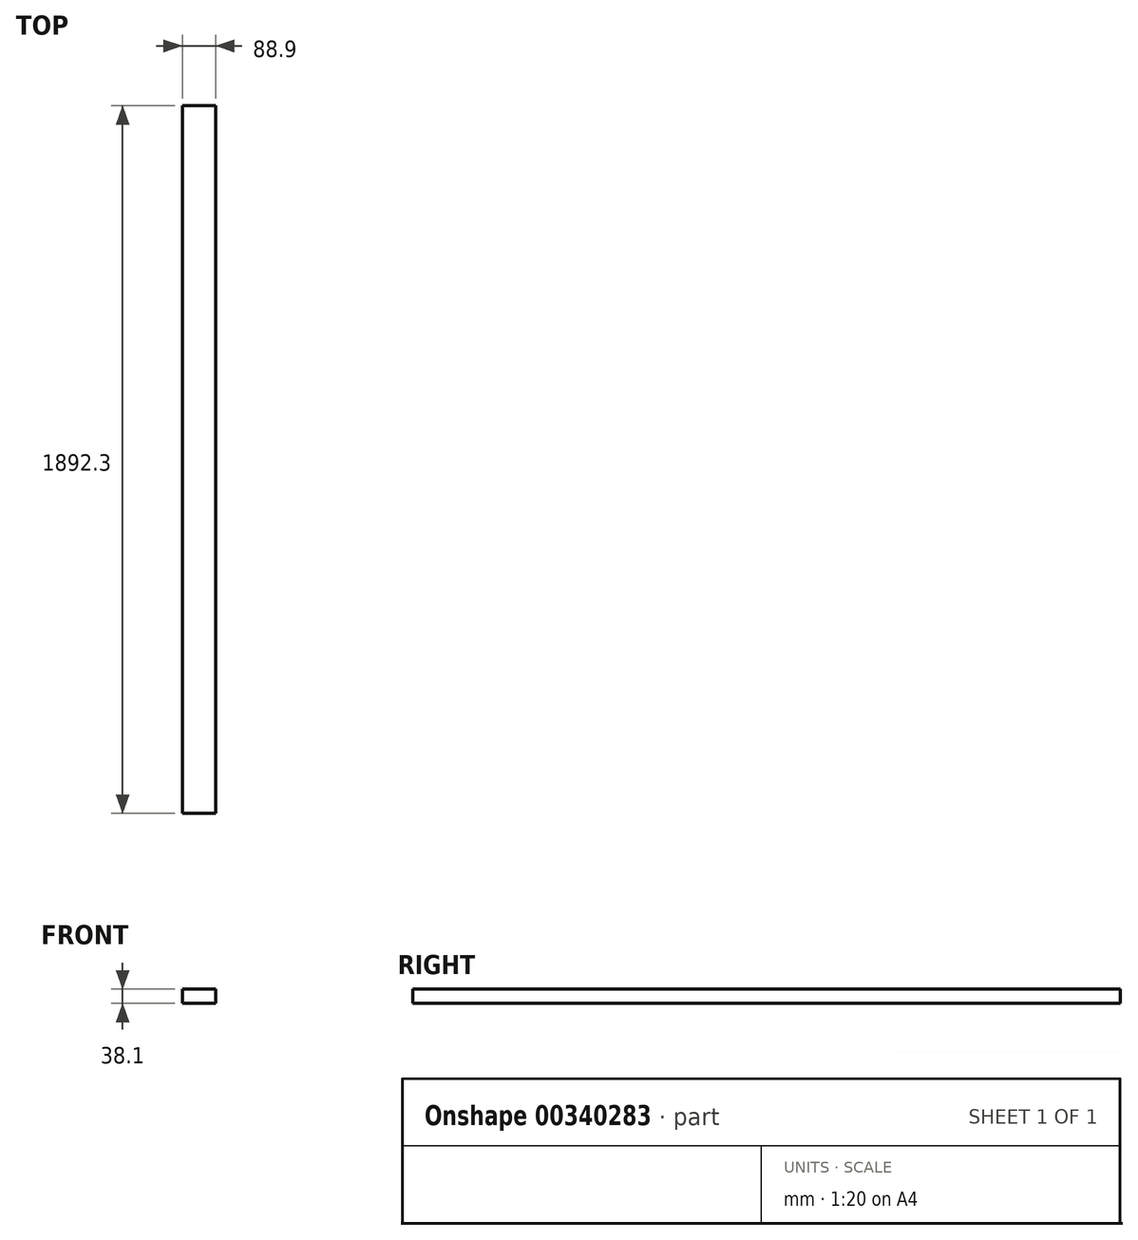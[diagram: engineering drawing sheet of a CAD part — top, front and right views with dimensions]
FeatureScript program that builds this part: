
annotation { "Feature Type Name" : "Feature", "Feature Type Description" : "" }
export const myFeature = defineFeature(function(context is Context, id is Id, definition is map)
    precondition{}
    {
        {
            var Q0;
            Q0=qCreatedBy(makeId("Front.planeOp"),FACE);
            var sketch = newSketch(context, id + "F0", { "sketchPlane" : qUnion([Q0])});
            skLineSegment(sketch, "E0.bottom", {"start": v(44.45, -19.05) * mm, "end": v(-44.45, -19.05) * mm});
            skLineSegment(sketch, "E0.top", {"start": v(44.45, 19.05) * mm, "end": v(-44.45, 19.05) * mm});
            skLineSegment(sketch, "E0.left", {"start": v(44.45, -19.05) * mm, "end": v(44.45, 19.05) * mm});
            skLineSegment(sketch, "E0.right", {"start": v(-44.45, -19.05) * mm, "end": v(-44.45, 19.05) * mm});
            skPoint(sketch, "E0.middle", {"position": v(0, 0) * mm});
            skSolve(sketch);
        }
        {
            var Q0;
            Q0=qSketchRegion(id+"F0",true);
            extrude(context, id + "F1", {"entities" : qUnion([Q0]), "endBound" : BoundingType.SYMMETRIC, "depth" : 1892.3 * mm});
        }
    });
